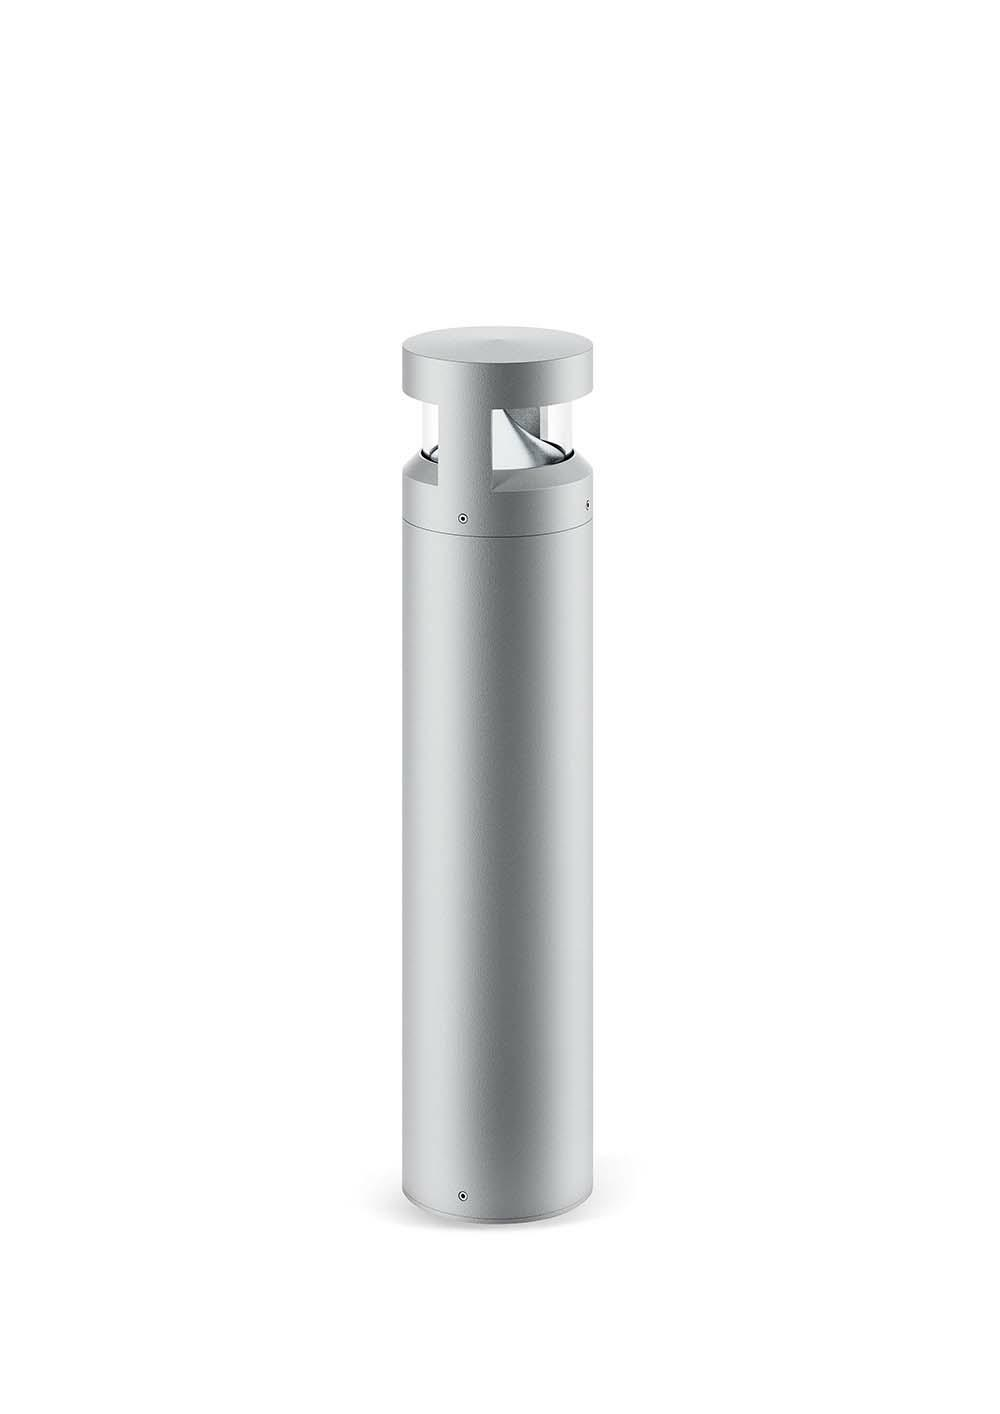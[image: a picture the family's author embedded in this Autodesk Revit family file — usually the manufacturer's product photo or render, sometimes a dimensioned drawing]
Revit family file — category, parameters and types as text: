
# Revit family: Platek_Mirco Menhir_2_Openings
name_source: partatom
category: Apparecchi per illuminazione
revit_build: Autodesk Revit 2017 (Build: 20160225_1515(x64)
units: mm (PartAtom-declared; Revit-internal decimal feet)

## family parameters
Basato su piano di lavoro = Sì
Condiviso = Sì
Punto di calcolo locali = No
Quota connettore circolare = Usa diametro
Sempre verticale = No
Sorgente d'illuminazione = No
Taglio con vuoti quando caricato = No
Tipo di parte = Normale

## types (3) — shared parameters
Aluminium = PLK_Aluminium
Body = PLK_Grey
CRI = >80
Carico apparente = 0 VA
Colour Temperature = 3000 K
Commenti sul tipo = Pedestrian areas, Urban zones, Paths, Roads
Descrizione = Outdoor Lighting, Floor/Ground Illumination
Diffuse Type = PMMA
Dimmable = Yes
Energy Efficiency Rating = A/A+/A++
Frequency = 50/60 Hz
IK Rating = IK 08
IP Rating = IP65
Insulation Class = 2
LED Protection = Surge protection included
Light Source = PLK_Light Source
Manufacturer Comment = 4mm Thick PMMA
Modello = MICRO MENHIR
Mounting Type = Ground
Nota chiave = Other Led colors available on request, IP68 connector included
PLATEK FInishes = Painted Aluminium, Avalaible in Grey/White/Bronze/Black/Anthracite
Power Supply Unit = Included
Product Documentation Link = http://www.platek.eu
Product Page URL = http://www.platek.eu
Produttore = PLATEK SRL
Prospetto di default = 1219 mm
Supply Voltage = 230 V
Supply Voltage Max = 240 V
Supply Voltage Min = 220 V
URL = www.platek.eu

## per-type parameters (varying)
| type | Angolo di inclinazione | Codice assieme | Height | Height150 | Height500 | Height800 | Immagine tipo | Lampada | Luminaire Luminous Flux | Luminaire Luminous Intensity | Luminaire Wattage | PLATEK Article Code | PLK_Photometric | Product Dimension |
| 4011112_9,6W_LED_3000K_H150mm | 0.00° | 4011112.06(Grey); 4011112.08(Anthracite); 3440519.01(Black); 4011112.02(White); 4011112.07(Corten); 4011112.09(Bronze) | 43 mm  [stored 0.141076 ft] | Sì | No | No | micro_menhir_15_01.jpg | LED | 500 lm | 197 cd | 10 W | 4011112 | PLK_Photometrics_4011112 | D115mm x H150mm |
| 4011312_13,5W_LED_3000K_H800mm | 90.00° | 4011312.06(Grey); 4011312.08(Anthracite); 4011312.01(Black);  4011312.01(Black);  4011312.02(White);  4011312.07(Corten);  4011312.09(Bronze) | 703 mm  [stored 2.30643 ft] | No | No | Sì | micro_menhir_80.jpg | 2 LED | 665 lm | 265 cd | 14 W | 4011312 | PLK_Photometrics_4011212 | D115mm x H800mm |
| 4011212_13,5W_LED_3000K_H500mm | 90.00° | 4011212.06(Grey); 4011212.08(Anthracite); 4011212.01(Black); 4011212.02(White); 4011212.07(Corten); 4011212.09(Bronze) | 403 mm  [stored 1.32218 ft] | No | Sì | No | micro_menhir_50.jpg | 2 LED | 665 lm | 265 cd | 14 W | 4011212 | PLK_Photometrics_4011212 | D115mm x H500mm |

note: [stored X ft] marks values corroborated as IEEE doubles in the binary element streams (Revit-internal decimal feet)
